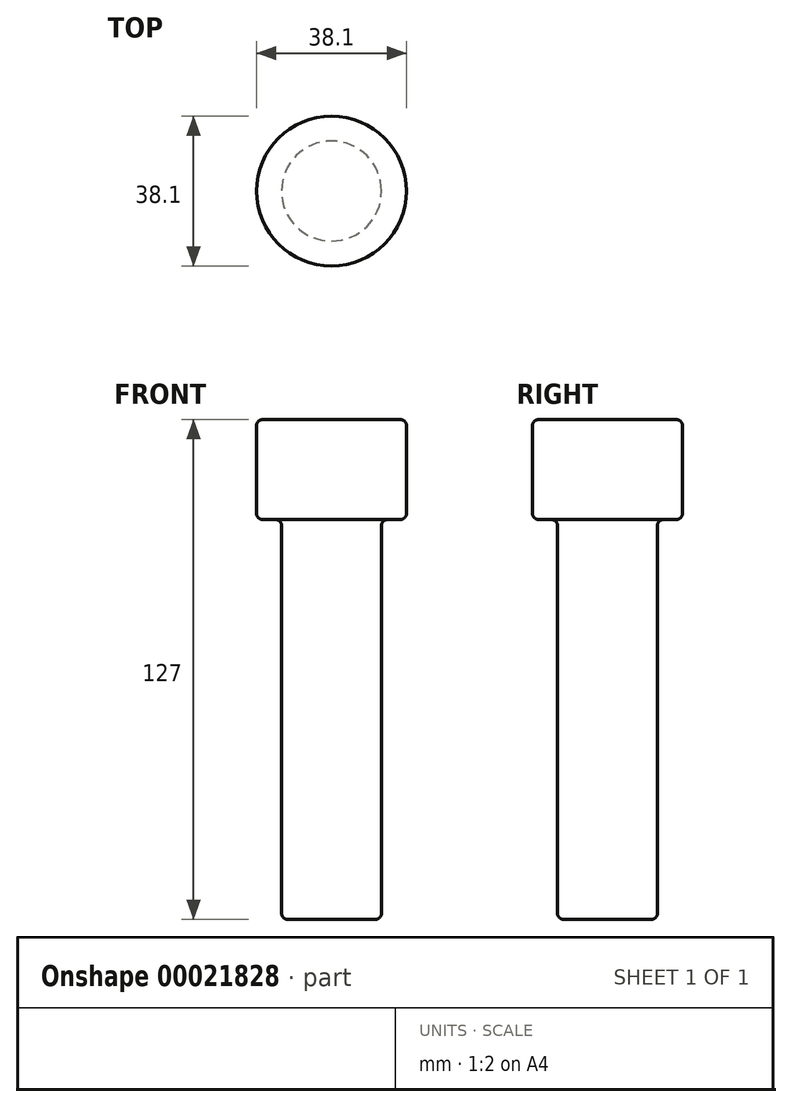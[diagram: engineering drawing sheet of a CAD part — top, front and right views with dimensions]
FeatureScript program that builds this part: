
annotation { "Feature Type Name" : "Feature", "Feature Type Description" : "" }
export const myFeature = defineFeature(function(context is Context, id is Id, definition is map)
    precondition{}
    {
        {
            var Q0;
            Q0=qCreatedBy(makeId("Top.planeOp"),FACE);
            var sketch = newSketch(context, id + "F0", { "sketchPlane" : qUnion([Q0])});
            skCircle(sketch, "E0", {"center": v(0, 0) * mm, "radius": 19.05 * mm});
            skCircle(sketch, "E1", {"center": v(0, 0) * mm, "radius": 12.7 * mm});
            skSolve(sketch);
        }
        {
            var Q0;
            Q0=makeQuery(id+"F0.imprint","IMPRINT",FACE,{"disambiguationData":[TD([[makeQuery(id+"F0.imprint","IMPRINT",EDGE,{"derivedFrom":sQuery(id+"F0.wireOp",EDGE,"E0")}),1.0]])]});
            var Q1;
            Q1=makeQuery(id+"F0.imprint","IMPRINT",FACE,{"disambiguationData":[TD([[makeQuery(id+"F0.imprint","IMPRINT",EDGE,{"derivedFrom":sQuery(id+"F0.wireOp",EDGE,"E1")}),1.0]])]});
            extrude(context, id + "F1", {"entities" : qUnion([Q0, Q1]), "depth" : 25.4 * mm});
        }
        {
            var Q0;
            Q0=makeQuery(id+"F0.imprint","IMPRINT",FACE,{"disambiguationData":[TD([[makeQuery(id+"F0.imprint","IMPRINT",EDGE,{"derivedFrom":sQuery(id+"F0.wireOp",EDGE,"E1")}),1.0]])]});
            var Q1;
            Q1=sQuery(id+"F0.wireOp",EDGE,"E1");
            extrude(context, id + "F2", {"entities" : qUnion([Q0]), "operationType" : NewBodyOperationType.ADD, "surfaceEntities" : qUnion([Q1]), "oppositeDirection" : true, "depth" : 101.6 * mm});
        }
        {
            var Q0;
            Q0=makeQuery(id+"F1.opExtrude","SWEPT_FACE",FACE,{"disambiguationData":[OSD([sQuery(id+"F0.wireOp",EDGE,"E0")])]});
            var Q1;
            Q1=makeQuery(id+"F2.opExtrude","SWEPT_FACE",FACE,{"disambiguationData":[OSD([sQuery(id+"F0.wireOp",EDGE,"E1")])]});
            fillet(context, id + "F3", {"entities" : qUnion([Q0, Q1]), "radius" : 1.59 * mm, "tangentPropagation" : true, "allowEdgeOverflow" : false});
        }
    });
